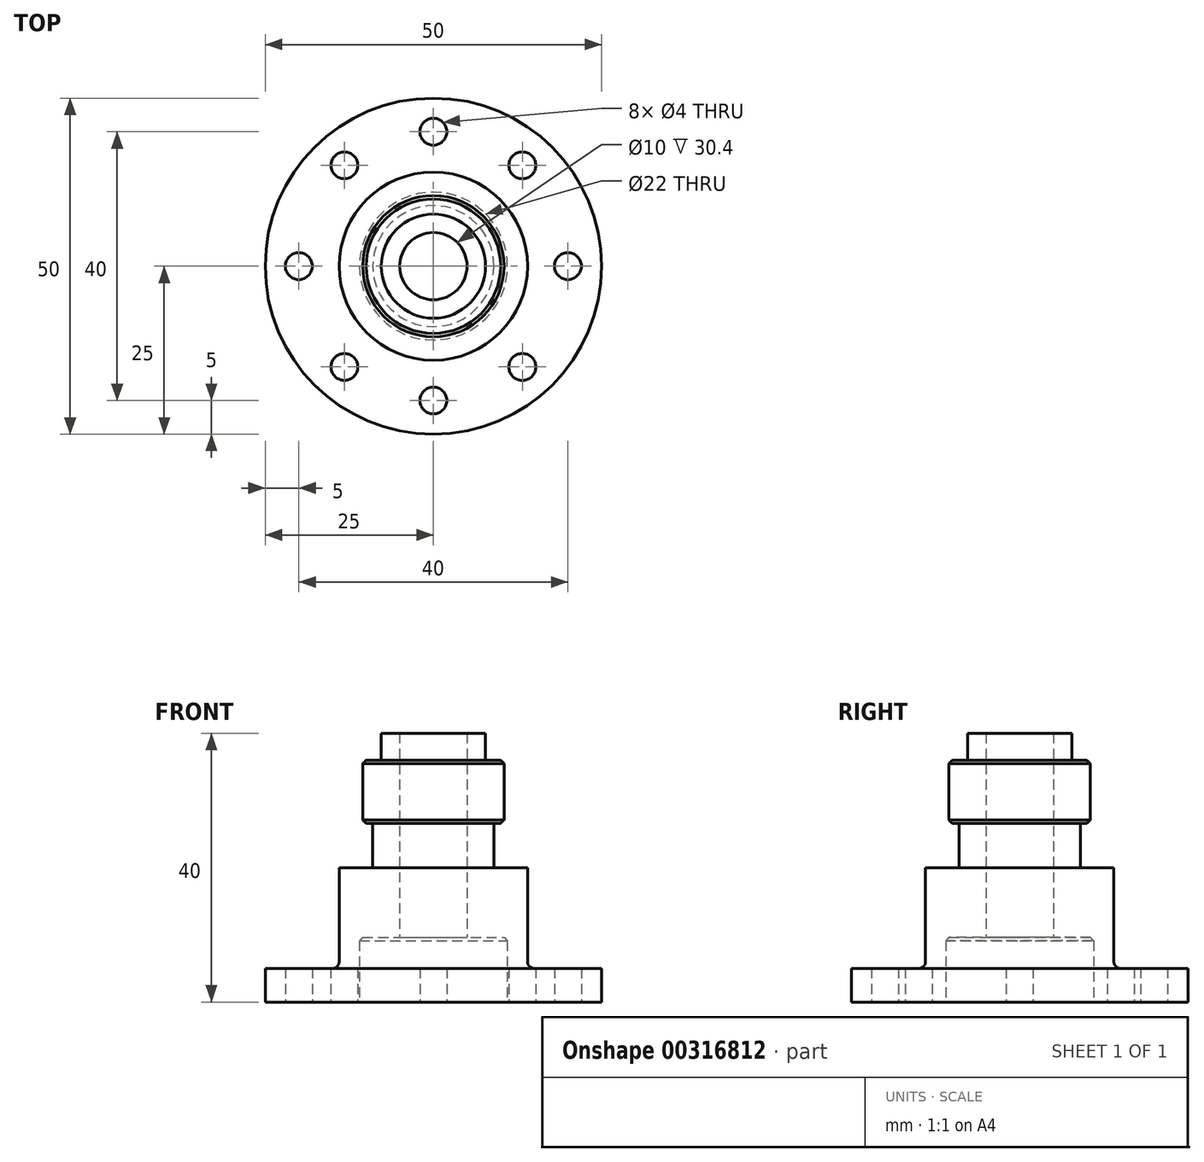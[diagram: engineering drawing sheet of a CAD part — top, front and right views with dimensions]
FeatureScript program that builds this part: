
annotation { "Feature Type Name" : "Feature", "Feature Type Description" : "" }
export const myFeature = defineFeature(function(context is Context, id is Id, definition is map)
    precondition{}
    {
        {
            var Q0;
            Q0=qCreatedBy(makeId("Front.planeOp"),FACE);
            var sketch = newSketch(context, id + "F0", { "sketchPlane" : qUnion([Q0])});
            skLineSegment(sketch, "E0", {"start": v(0, 0) * mm, "end": v(7.75, 0) * mm});
            skLineSegment(sketch, "E1", {"start": v(7.75, 0) * mm, "end": v(7.75, -4) * mm});
            skLineSegment(sketch, "E2", {"start": v(7.75, -4) * mm, "end": v(10.5, -4) * mm});
            skLineSegment(sketch, "E3", {"start": v(10.5, -4) * mm, "end": v(10.5, -13.4) * mm});
            skLineSegment(sketch, "E4", {"start": v(10.5, -13.4) * mm, "end": v(9, -13.4) * mm});
            skLineSegment(sketch, "E5", {"start": v(9, -13.4) * mm, "end": v(9, -20) * mm});
            skLineSegment(sketch, "E6", {"start": v(9, -20) * mm, "end": v(14, -20) * mm});
            skLineSegment(sketch, "E7", {"start": v(14, -20) * mm, "end": v(14, -34) * mm});
            skLineSegment(sketch, "E8", {"start": v(15, -35) * mm, "end": v(25, -35) * mm});
            skLineSegment(sketch, "E9", {"start": v(25, -35) * mm, "end": v(25, -40) * mm});
            skLineSegment(sketch, "E10", {"start": v(25, -40) * mm, "end": v(0, -40) * mm});
            skLineSegment(sketch, "E11", {"start": v(0, -40) * mm, "end": v(0, 0) * mm});
            skPoint(sketch, "E12.visualSharp", {"position": v(14, -35) * mm});
            skArc(sketch, "E12.filletArc", {"start": v(14, -34) * mm, "mid": v(14.3, -34.7) * mm, "end": v(15, -35) * mm});
            skSolve(sketch);
        }
        {
            var Q0;
            Q0 = qSketchRegion(id + "F0", true);
            var Q1;
            Q1=sQuery(id+"F0.wireOp",EDGE,"E11");
            revolve(context, id + "F1", {"entities" : qUnion([Q0]), "axis" : qUnion([Q1]), "revolveType" : RevolveType.FULL});
        }
        {
            var Q0;
            Q0=makeQuery(id+"F1.opRevolve","SWEPT_FACE",FACE,{"disambiguationData":[OSD([sQuery(id+"F0.wireOp",EDGE,"E10")])]});
            var sketch = newSketch(context, id + "F2", { "sketchPlane" : qUnion([Q0])});
            skCircle(sketch, "E13", {"center": v(0, 0) * mm, "radius": 20 * mm, "construction": true});
            skCircle(sketch, "E14", {"center": v(0, 0) * mm, "radius": 11 * mm});
            skCircle(sketch, "E15", {"center": v(0, 0) * mm, "radius": 5 * mm});
            skCircle(sketch, "E16", {"center": v(20, 0) * mm, "radius": 2 * mm});
            skCircle(sketch, "E17", {"center": v(-20, 0) * mm, "radius": 2 * mm});
            skCircle(sketch, "E18", {"center": v(0, -20) * mm, "radius": 2 * mm});
            skCircle(sketch, "E19", {"center": v(0, 20) * mm, "radius": 2 * mm});
            skCircle(sketch, "E20", {"center": v(13.23, 15) * mm, "radius": 2 * mm});
            skCircle(sketch, "E21", {"center": v(13.23, -15) * mm, "radius": 2 * mm});
            skCircle(sketch, "E22", {"center": v(-13.23, -15) * mm, "radius": 2 * mm});
            skCircle(sketch, "E23", {"center": v(-13.23, 15) * mm, "radius": 2 * mm});
            skSolve(sketch);
        }
        {
            var Q0;
            Q0=makeQuery(id+"F2.imprint","IMPRINT",FACE,{"disambiguationData":[TD([[makeQuery(id+"F2.imprint","IMPRINT",EDGE,{"derivedFrom":sQuery(id+"F2.wireOp",EDGE,"E15")}),1.0]])]});
            extrude(context, id + "F3", {"entities" : qUnion([Q0]), "operationType" : NewBodyOperationType.REMOVE, "oppositeDirection" : true, "depth" : 40 * mm});
        }
        {
            var Q0;
            Q0=makeQuery(id+"F2.imprint","IMPRINT",FACE,{"disambiguationData":[TD([[makeQuery(id+"F2.imprint","IMPRINT",EDGE,{"derivedFrom":sQuery(id+"F2.wireOp",EDGE,"E14")}),1.0]])]});
            extrude(context, id + "F4", {"entities" : qUnion([Q0]), "operationType" : NewBodyOperationType.REMOVE, "oppositeDirection" : true, "depth" : 9.6 * mm});
        }
        {
            var Q0;
            Q0=makeQuery(id+"F2.imprint","IMPRINT",FACE,{"disambiguationData":[TD([[makeQuery(id+"F2.imprint","IMPRINT",EDGE,{"derivedFrom":sQuery(id+"F2.wireOp",EDGE,"E23")}),1.0]])]});
            var Q1;
            Q1=makeQuery(id+"F2.imprint","IMPRINT",FACE,{"disambiguationData":[TD([[makeQuery(id+"F2.imprint","IMPRINT",EDGE,{"derivedFrom":sQuery(id+"F2.wireOp",EDGE,"E19")}),1.0]])]});
            var Q2;
            Q2=makeQuery(id+"F2.imprint","IMPRINT",FACE,{"disambiguationData":[TD([[makeQuery(id+"F2.imprint","IMPRINT",EDGE,{"derivedFrom":sQuery(id+"F2.wireOp",EDGE,"E20")}),1.0]])]});
            var Q3;
            Q3=makeQuery(id+"F2.imprint","IMPRINT",FACE,{"disambiguationData":[TD([[makeQuery(id+"F2.imprint","IMPRINT",EDGE,{"derivedFrom":sQuery(id+"F2.wireOp",EDGE,"E16")}),1.0]])]});
            var Q4;
            Q4=makeQuery(id+"F2.imprint","IMPRINT",FACE,{"disambiguationData":[TD([[makeQuery(id+"F2.imprint","IMPRINT",EDGE,{"derivedFrom":sQuery(id+"F2.wireOp",EDGE,"E21")}),1.0]])]});
            var Q5;
            Q5=makeQuery(id+"F2.imprint","IMPRINT",FACE,{"disambiguationData":[TD([[makeQuery(id+"F2.imprint","IMPRINT",EDGE,{"derivedFrom":sQuery(id+"F2.wireOp",EDGE,"E18")}),1.0]])]});
            var Q6;
            Q6=makeQuery(id+"F2.imprint","IMPRINT",FACE,{"disambiguationData":[TD([[makeQuery(id+"F2.imprint","IMPRINT",EDGE,{"derivedFrom":sQuery(id+"F2.wireOp",EDGE,"E22")}),1.0]])]});
            var Q7;
            Q7=makeQuery(id+"F2.imprint","IMPRINT",FACE,{"disambiguationData":[TD([[makeQuery(id+"F2.imprint","IMPRINT",EDGE,{"derivedFrom":sQuery(id+"F2.wireOp",EDGE,"E17")}),1.0]])]});
            extrude(context, id + "F5", {"entities" : qUnion([Q0, Q1, Q2, Q3, Q4, Q5, Q6, Q7]), "operationType" : NewBodyOperationType.REMOVE, "oppositeDirection" : true, "depth" : 5 * mm});
        }
        {
            var Q0;
            Q0=makeQuery(id+"F1.opRevolve","SWEPT_EDGE",EDGE,{"disambiguationData":[OSD([sQuery(id+"F0.wireOp",EDGE,"E3"),sQuery(id+"F0.wireOp",EDGE,"E4")])]});
            var Q1;
            Q1=makeQuery(id+"F1.opRevolve","SWEPT_EDGE",EDGE,{"disambiguationData":[OSD([sQuery(id+"F0.wireOp",EDGE,"E2"),sQuery(id+"F0.wireOp",EDGE,"E3")])]});
            var Q2;
            Q2=makeQuery(id+"F4.boolean.opBoolean","COPY",EDGE,{"derivedFrom":makeQuery(id+"F4.opExtrude","CAP_EDGE",EDGE,{"disambiguationData":[OSD([sQuery(id+"F2.wireOp",EDGE,"E14")])],"isStart":false})});
            chamfer(context, id + "F6", {"entities" : qUnion([Q0, Q1, Q2]), "width" : .5 * mm, "tangentPropagation" : true});
        }
    });
